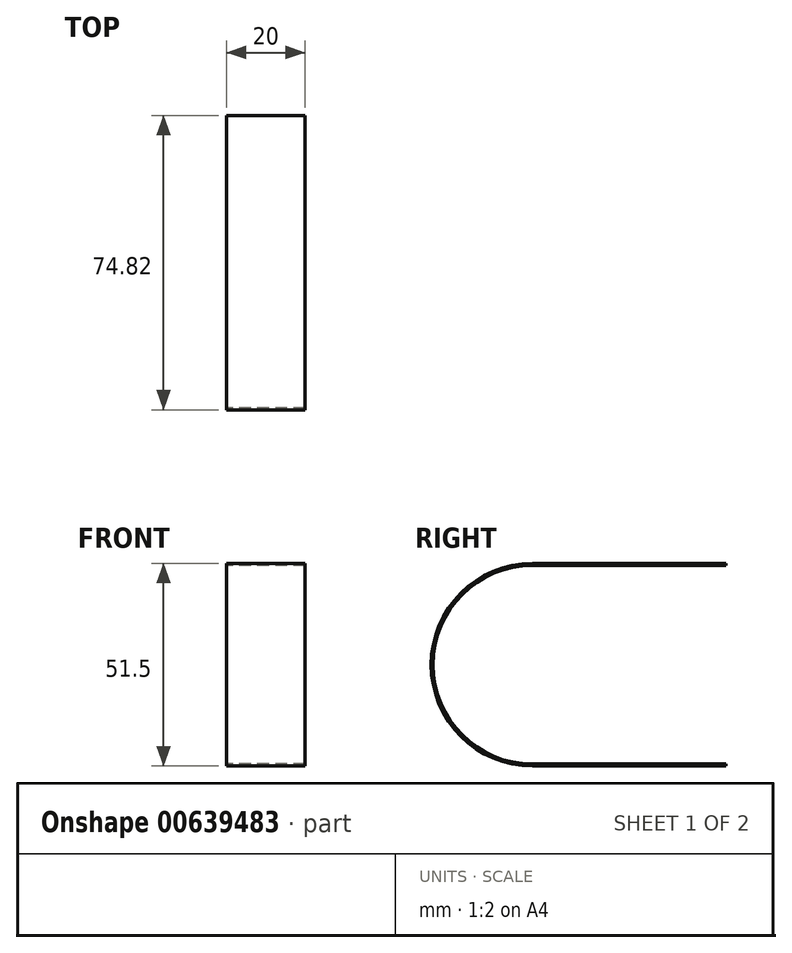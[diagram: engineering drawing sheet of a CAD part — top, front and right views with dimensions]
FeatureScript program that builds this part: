
annotation { "Feature Type Name" : "Feature", "Feature Type Description" : "" }
export const myFeature = defineFeature(function(context is Context, id is Id, definition is map)
    precondition{}
    {
        {
            var Q0;
            Q0=qCreatedBy(makeId("Right.planeOp"),FACE);
            var sketch = newSketch(context, id + "F0", { "sketchPlane" : qUnion([Q0])});
            skCircle(sketch, "E0", {"center": v(0, 0) * mm, "radius": 25 * mm});
            skSolve(sketch);
        }
        {
            var Q0;
            Q0=makeQuery(id+"F0.imprint","IMPRINT",FACE,{"disambiguationData":[TD([[makeQuery(id+"F0.imprint","IMPRINT",EDGE,{"derivedFrom":sQuery(id+"F0.wireOp",EDGE,"E0")}),1.0]])]});
            extrude(context, id + "F1", {"entities" : qUnion([Q0]), "depth" : 15 * mm, "offsetDistance" : 25 * mm});
        }
        {
            var Q0;
            Q0=qCreatedBy(makeId("Right.planeOp"),FACE);
            var sketch = newSketch(context, id + "F2", { "sketchPlane" : qUnion([Q0])});
            skCircle(sketch, "E1.0", {"center": v(0, 0) * mm, "radius": 25 * mm});
            skArc(sketch, "E2", {"start": v(0, 25.25) * mm, "mid": v(-25.25, 0) * mm, "end": v(0, -25.25) * mm});
            skArc(sketch, "E3", {"start": v(0, 25.75) * mm, "mid": v(-25.75, 0) * mm, "end": v(0, -25.75) * mm});
            skLineSegment(sketch, "E4", {"start": v(-25.75, 0) * mm, "end": v(-25.25, 0) * mm});
            skLineSegment(sketch, "E5", {"start": v(25.25, 0) * mm, "end": v(25.75, 0) * mm});
            skLineSegment(sketch, "E6", {"start": v(0, -25.25) * mm, "end": v(49.07, -25.25) * mm});
            skLineSegment(sketch, "E7", {"start": v(0, -25.75) * mm, "end": v(49.07, -25.75) * mm});
            skLineSegment(sketch, "E8", {"start": v(49.07, -25.75) * mm, "end": v(49.07, -25.25) * mm});
            skLineSegment(sketch, "E9", {"start": v(0, 25.75) * mm, "end": v(49.07, 25.75) * mm});
            skLineSegment(sketch, "E10", {"start": v(0, 25.25) * mm, "end": v(49.07, 25.25) * mm});
            skLineSegment(sketch, "E11", {"start": v(49.07, 25.25) * mm, "end": v(49.07, 25.75) * mm});
            skSolve(sketch);
        }
        {
            var Q0;
            Q0=makeQuery(id+"F1.opExtrude","CAP_FACE",FACE,{"disambiguationData":[OSD([sQuery(id+"F0.wireOp",EDGE,"E0")])],"isStart":false});
            extrude(context, id + "F3", {"entities" : qUnion([Q0]), "operationType" : NewBodyOperationType.REMOVE, "oppositeDirection" : true, "depth" : 25 * mm, "offsetDistance" : 25 * mm});
        }
        {
            var Q0;
            {var subQ1=sQuery(id+"F2.wireOp",EDGE,"E4");Q0=makeQuery(id+"F2.imprint","IMPRINT",FACE,{"disambiguationData":[TD([[makeQuery(id+"F2.imprint","IMPRINT",EDGE,{"derivedFrom":subQ1}),1.0]])]});}
            var Q1;
            {var subQ1=sQuery(id+"F2.wireOp",EDGE,"E4");Q1=makeQuery(id+"F2.imprint","IMPRINT",FACE,{"disambiguationData":[TD([[makeQuery(id+"F2.imprint","IMPRINT",EDGE,{"derivedFrom":subQ1}),-1.0]])]});}
            extrude(context, id + "F4", {"entities" : qUnion([Q0, Q1]), "depth" : 20 * mm, "offsetDistance" : 25 * mm});
        }
    });
